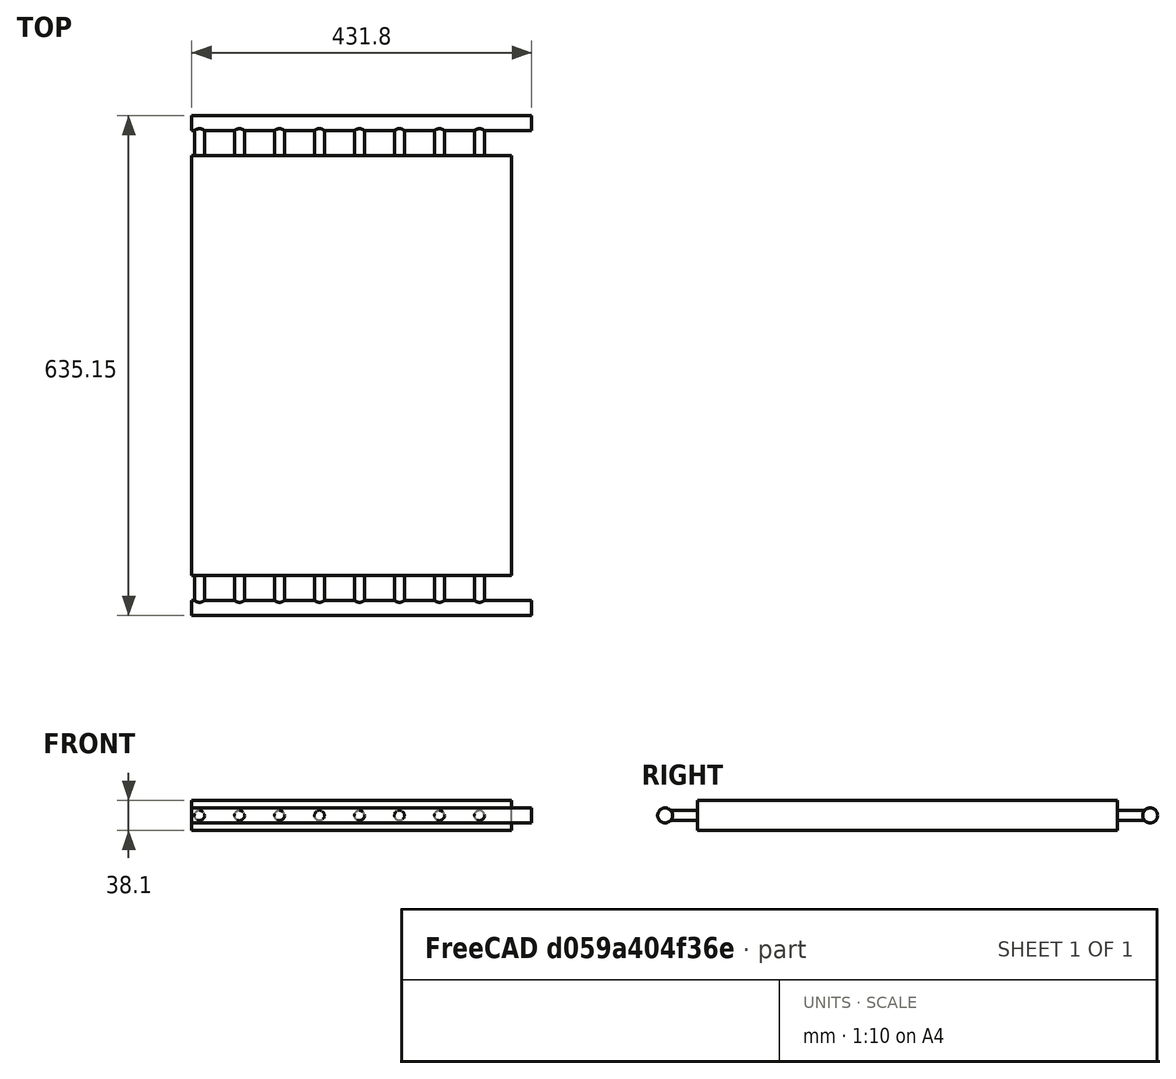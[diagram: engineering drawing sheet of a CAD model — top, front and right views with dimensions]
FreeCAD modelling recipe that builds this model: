
FCSTD DOCUMENT  (FreeCAD 0.16R6712 (Git))
Label: oil cooler
License: All rights reserved
LicenseURL: http://en.wikipedia.org/wiki/All_rights_reserved
objects: App::FeaturePython×10, Part::FeaturePython×8, Part::Cylinder×2, Part::Box×1, Part::MultiFuse×1
note: 12 computed .brp shape members not serialized (recipe doc carries the construction recipe); baked Part::Feature solids carry a one-line shape summary decoded from their .brp

FEATURE [Part::Cylinder] cylinder  label="distribution 01"
  Angle = 360
  Height = 431.8
  Placement = pos=(-84.2,-176.226,6.35) rot=(0.57735,-0.57735,0.57735;4.18879rad)
  Radius = 9.525
FEATURE [Part::Cylinder] cylinder002  label="exchange 01"
  Angle = 360
  Height = 615.95
  Placement = pos=(-74.4,436.46,6.35) rot=(1,0,0;1.5708rad)
  Radius = 6.35
FEATURE [Part::Box] cube  label="fins"
  Height = 38.1
  Length = 406.4
  Placement = pos=(-84.2,-135.04,-12.7) rot=(0,0,1;0rad)
  Width = 533.4
FEATURE [App::FeaturePython] planeConstraint01  label="exchange tube 01 to side"  # a2plus constraint (typed FeaturePython)
  Object1 = cylinder002
  Object2 = cube
  SubElement1 = Face2
  SubElement2 = Face3
  Type = plane
  directionConstraint = 1
  offset = 44.45
FEATURE [Part::FeaturePython] Clone  label="Clone of exchange001"  # Draft clone (typed FeaturePython)
  Objects = -> [cylinder002]
  Placement = pos=(27.2,436.46,6.35) rot=(1,0,0;1.5708rad)
  Scale = (1,1,1)
FEATURE [Part::FeaturePython] Clone002  label="Clone of exchange002"  # Draft clone (typed FeaturePython)
  Objects = -> [cylinder002]
  Placement = pos=(78,436.46,6.35) rot=(1,0,0;1.5708rad)
  Scale = (1,1,1)
FEATURE [Part::FeaturePython] Clone003  label="Clone of exchange003"  # Draft clone (typed FeaturePython)
  Objects = -> [cylinder002]
  Placement = pos=(128.8,436.46,6.35) rot=(1,0,0;1.5708rad)
  Scale = (1,1,1)
FEATURE [Part::FeaturePython] Clone004  label="Clone of exchange004"  # Draft clone (typed FeaturePython)
  Objects = -> [cylinder002]
  Placement = pos=(179.6,436.46,6.35) rot=(1,0,0;1.5708rad)
  Scale = (1,1,1)
FEATURE [Part::FeaturePython] Clone005  label="Clone of exchange005"  # Draft clone (typed FeaturePython)
  Objects = -> [cylinder002]
  Placement = pos=(230.4,436.46,6.35) rot=(1,0,0;1.5708rad)
  Scale = (1,1,1)
FEATURE [Part::FeaturePython] Clone006  label="Clone of exchange006"  # Draft clone (typed FeaturePython)
  Objects = -> [cylinder002]
  Placement = pos=(281.2,436.46,6.35) rot=(1,0,0;1.5708rad)
  Scale = (1,1,1)
FEATURE [Part::FeaturePython] Clone007  label="Clone of exchange"  # Draft clone (typed FeaturePython)
  Objects = -> [cylinder002]
  Placement = pos=(-23.6,436.46,6.35) rot=(1,0,0;1.5708rad)
  Scale = (1,1,1)
FEATURE [Part::FeaturePython] Clone008  label="Clone of distribution"  # Draft clone (typed FeaturePython)
  Objects = -> [cylinder]
  Placement = pos=(-84.2,439.876,6.35) rot=(0.57735,-0.57735,0.57735;4.18879rad)
  Scale = (1,1,1)
FEATURE [App::FeaturePython] planeConstraint02  label="distro to fin bottom"  # a2plus constraint (typed FeaturePython)
  Object1 = cylinder
  Object2 = cube
  SubElement1 = Face3
  SubElement2 = Face1
  Type = plane
  directionConstraint = 0
  offset = 0
FEATURE [App::FeaturePython] planeConstraint03  label="distro clone to distro"  # a2plus constraint (typed FeaturePython)
  Object1 = Clone008
  Object2 = cylinder
  SubElement1 = Face3
  SubElement2 = Face3
  Type = plane
  directionConstraint = 0
  offset = 0
FEATURE [App::FeaturePython] planeConstraint04  label="ends of clones of exchange to exchange 01"  # a2plus constraint (typed FeaturePython)
  Object1 = Clone006
  Object2 = cylinder002
  SubElement1 = Face2
  SubElement2 = Face2
  Type = plane
  directionConstraint = 0
  offset = 0
FEATURE [App::FeaturePython] planeConstraint05  # a2plus constraint (typed FeaturePython)
  Object1 = Clone005
  Object2 = cylinder002
  SubElement1 = Face2
  SubElement2 = Face2
  Type = plane
  directionConstraint = 0
  offset = 0
FEATURE [App::FeaturePython] planeConstraint06  # a2plus constraint (typed FeaturePython)
  Object1 = Clone004
  Object2 = cylinder002
  SubElement1 = Face2
  SubElement2 = Face2
  Type = plane
  directionConstraint = 0
  offset = 0
FEATURE [App::FeaturePython] planeConstraint07  # a2plus constraint (typed FeaturePython)
  Object1 = Clone003
  Object2 = cylinder002
  SubElement1 = Face2
  SubElement2 = Face2
  Type = plane
  directionConstraint = 0
  offset = 0
FEATURE [App::FeaturePython] planeConstraint08  # a2plus constraint (typed FeaturePython)
  Object1 = Clone002
  Object2 = cylinder002
  SubElement1 = Face2
  SubElement2 = Face2
  Type = plane
  directionConstraint = 0
  offset = 0
FEATURE [App::FeaturePython] planeConstraint09  # a2plus constraint (typed FeaturePython)
  Object1 = Clone
  Object2 = cylinder002
  SubElement1 = Face2
  SubElement2 = Face2
  Type = plane
  directionConstraint = 0
  offset = 0
FEATURE [App::FeaturePython] planeConstraint10  # a2plus constraint (typed FeaturePython)
  Object1 = Clone007
  Object2 = cylinder002
  SubElement1 = Face2
  SubElement2 = Face2
  Type = plane
  directionConstraint = 0
  offset = 0
FEATURE [Part::MultiFuse] Fusion  label="Oil Cooler Hayden 1284"
  Shapes = -> [cylinder,Clone006,Clone003,Clone,Clone005,cube,Clone007,cylinder002,Clone008,Clone002,Clone004]
